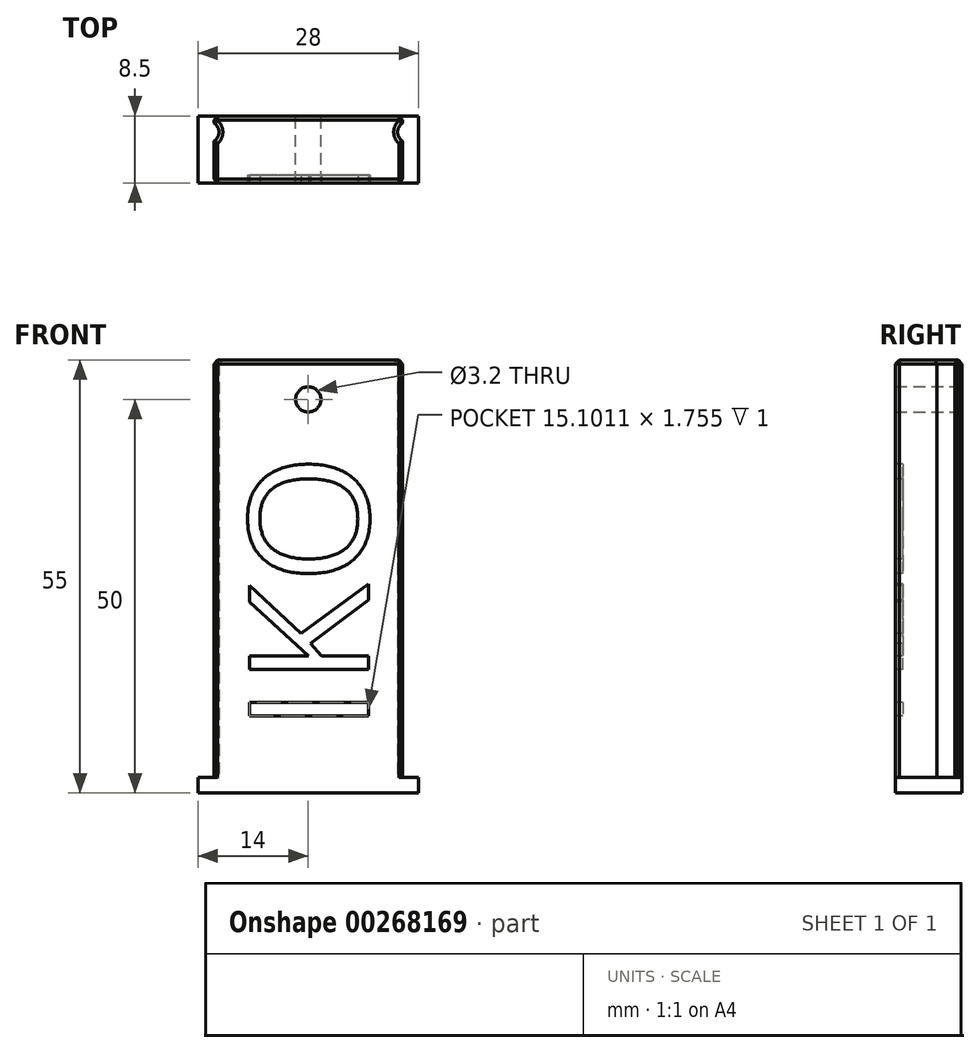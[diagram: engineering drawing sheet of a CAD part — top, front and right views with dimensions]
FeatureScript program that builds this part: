
annotation { "Feature Type Name" : "Feature", "Feature Type Description" : "" }
export const myFeature = defineFeature(function(context is Context, id is Id, definition is map)
    precondition{}
    {
        {
            var Q0;
            Q0=qCreatedBy(makeId("Top.planeOp"),FACE);
            var sketch = newSketch(context, id + "F0", { "sketchPlane" : qUnion([Q0])});
            skLineSegment(sketch, "E0.bottom", {"start": v(14, -4.25) * mm, "end": v(-14, -4.25) * mm});
            skLineSegment(sketch, "E0.top", {"start": v(14, 4.25) * mm, "end": v(-14, 4.25) * mm});
            skLineSegment(sketch, "E0.left", {"start": v(14, -4.25) * mm, "end": v(14, 4.25) * mm});
            skLineSegment(sketch, "E0.right", {"start": v(-14, -4.25) * mm, "end": v(-14, 4.25) * mm});
            skPoint(sketch, "E0.middle", {"position": v(0, 0) * mm});
            skSolve(sketch);
        }
        {
            var Q0;
            Q0 = qSketchRegion(id + "F0", true);
            extrude(context, id + "F1", {"entities" : qUnion([Q0]), "depth" : 2 * mm});
        }
        {
            var Q0;
            Q0=makeQuery(id+"F1.opExtrude","CAP_FACE",FACE,{"disambiguationData":[OSD([sQuery(id+"F0.wireOp",EDGE,"E0.bottom"),sQuery(id+"F0.wireOp",EDGE,"E0.top"),sQuery(id+"F0.wireOp",EDGE,"E0.left"),sQuery(id+"F0.wireOp",EDGE,"E0.right")])],"isStart":false});
            var sketch = newSketch(context, id + "F2", { "sketchPlane" : qUnion([Q0])});
            skLineSegment(sketch, "E1", {"start": v(-12, 4.25) * mm, "end": v(12, 4.25) * mm});
            skLineSegment(sketch, "E2", {"start": v(-12, -4.25) * mm, "end": v(12, -4.25) * mm});
            skLineSegment(sketch, "E3", {"start": v(12, 4.25) * mm, "end": v(12, 3.35) * mm});
            skLineSegment(sketch, "E4", {"start": v(12, -4.25) * mm, "end": v(12, 1.05) * mm});
            skLineSegment(sketch, "E5", {"start": v(-12, 4.25) * mm, "end": v(-12, 3.35) * mm});
            skLineSegment(sketch, "E6", {"start": v(-12, -4.25) * mm, "end": v(-12, 1.05) * mm});
            skLineSegment(sketch, "E7", {"start": v(22.82, 2.2) * mm, "end": v(-17.8, 2.2) * mm, "construction": true});
            skArc(sketch, "E8", {"start": v(12, 3.35) * mm, "mid": v(11.35, 2.2) * mm, "end": v(12, 1.05) * mm});
            skArc(sketch, "E9", {"start": v(-12, 1.05) * mm, "mid": v(-11.35, 2.2) * mm, "end": v(-12, 3.35) * mm});
            skPoint(sketch, "E10", {"position": v(12, 2.2) * mm});
            skSolve(sketch);
        }
        {
            var Q0;
            Q0 = qSketchRegion(id + "F2", true);
            extrude(context, id + "F3", {"entities" : qUnion([Q0]), "operationType" : NewBodyOperationType.ADD, "depth" : 53 * mm});
        }
        {
            var Q0;
            Q0=makeQuery(id+"F3.boolean.opBoolean","MERGE",FACE,{"derivedFrom":[makeQuery(id+"F1.opExtrude","SWEPT_FACE",FACE,{"disambiguationData":[OSD([sQuery(id+"F0.wireOp",EDGE,"E0.top")])]}),makeQuery(id+"F3.opExtrude","SWEPT_FACE",FACE,{"disambiguationData":[OSD([sQuery(id+"F2.wireOp",EDGE,"E1")])]})]});
            var sketch = newSketch(context, id + "F4", { "sketchPlane" : qUnion([Q0])});
            skCircle(sketch, "E11", {"center": v(0, 50) * mm, "radius": 1.6 * mm});
            skSolve(sketch);
        }
        {
            var Q0;
            Q0 = qSketchRegion(id + "F4", true);
            extrude(context, id + "F5", {"entities" : qUnion([Q0]), "operationType" : NewBodyOperationType.REMOVE, "endBound" : BoundingType.THROUGH_ALL, "oppositeDirection" : true, "depth" : 25 * mm});
        }
        {
            var Q0;
            Q0=makeQuery(id+"F3.opExtrude","CAP_FACE",FACE,{"disambiguationData":[OSD([sQuery(id+"F2.wireOp",EDGE,"E1"),sQuery(id+"F2.wireOp",EDGE,"E2"),sQuery(id+"F2.wireOp",EDGE,"E3"),sQuery(id+"F2.wireOp",EDGE,"E4"),sQuery(id+"F2.wireOp",EDGE,"E5"),sQuery(id+"F2.wireOp",EDGE,"E6"),sQuery(id+"F2.wireOp",EDGE,"E8"),sQuery(id+"F2.wireOp",EDGE,"E9")])],"isStart":false});
            var Q1;
            Q1=makeQuery(id+"F3.opExtrude","SWEPT_EDGE",EDGE,{"disambiguationData":[OSD([sQuery(id+"F0.wireOp",EDGE,"E0.top"),sQuery(id+"F2.wireOp",EDGE,"E1"),sQuery(id+"F2.wireOp",EDGE,"E5")])]});
            var Q2;
            Q2=makeQuery(id+"F3.opExtrude","SWEPT_EDGE",EDGE,{"disambiguationData":[OSD([sQuery(id+"F0.wireOp",EDGE,"E0.top"),sQuery(id+"F2.wireOp",EDGE,"E1"),sQuery(id+"F2.wireOp",EDGE,"E3")])]});
            var Q3;
            Q3=makeQuery(id+"F3.opExtrude","SWEPT_EDGE",EDGE,{"disambiguationData":[OSD([sQuery(id+"F0.wireOp",EDGE,"E0.bottom"),sQuery(id+"F2.wireOp",EDGE,"E2"),sQuery(id+"F2.wireOp",EDGE,"E6")])]});
            var Q4;
            Q4=makeQuery(id+"F3.opExtrude","SWEPT_EDGE",EDGE,{"disambiguationData":[OSD([sQuery(id+"F0.wireOp",EDGE,"E0.bottom"),sQuery(id+"F2.wireOp",EDGE,"E2"),sQuery(id+"F2.wireOp",EDGE,"E4")])]});
            chamfer(context, id + "F6", {"entities" : qUnion([Q0, Q1, Q2, Q3, Q4]), "width" : .5 * mm, "tangentPropagation" : true});
        }
        {
            var Q0;
            Q0=makeQuery(id+"F3.boolean.opBoolean","MERGE",FACE,{"derivedFrom":[makeQuery(id+"F1.opExtrude","SWEPT_FACE",FACE,{"disambiguationData":[OSD([sQuery(id+"F0.wireOp",EDGE,"E0.bottom")])]}),makeQuery(id+"F3.opExtrude","SWEPT_FACE",FACE,{"disambiguationData":[OSD([sQuery(id+"F2.wireOp",EDGE,"E2")])]})]});
            var sketch = newSketch(context, id + "F7", { "sketchPlane" : qUnion([Q0])});
            skText(sketch, "E12", { "text": "IKO", "fontName": "OpenSans-Regular.ttf"});
            skPoint(sketch, "E13", {"position": v(0, 43.14) * mm});
            const initialGuessF7  = {"E12": [0.00762, 0.0077, 0, 1, 0.01523]};
            skSetInitialGuess(sketch, initialGuessF7);
            skSolve(sketch);
        }
        {
            var Q0;
            Q0 = qSketchRegion(id + "F7", true);
            extrude(context, id + "F8", {"entities" : qUnion([Q0]), "operationType" : NewBodyOperationType.REMOVE, "oppositeDirection" : true, "depth" : 1 * mm});
        }
    });
